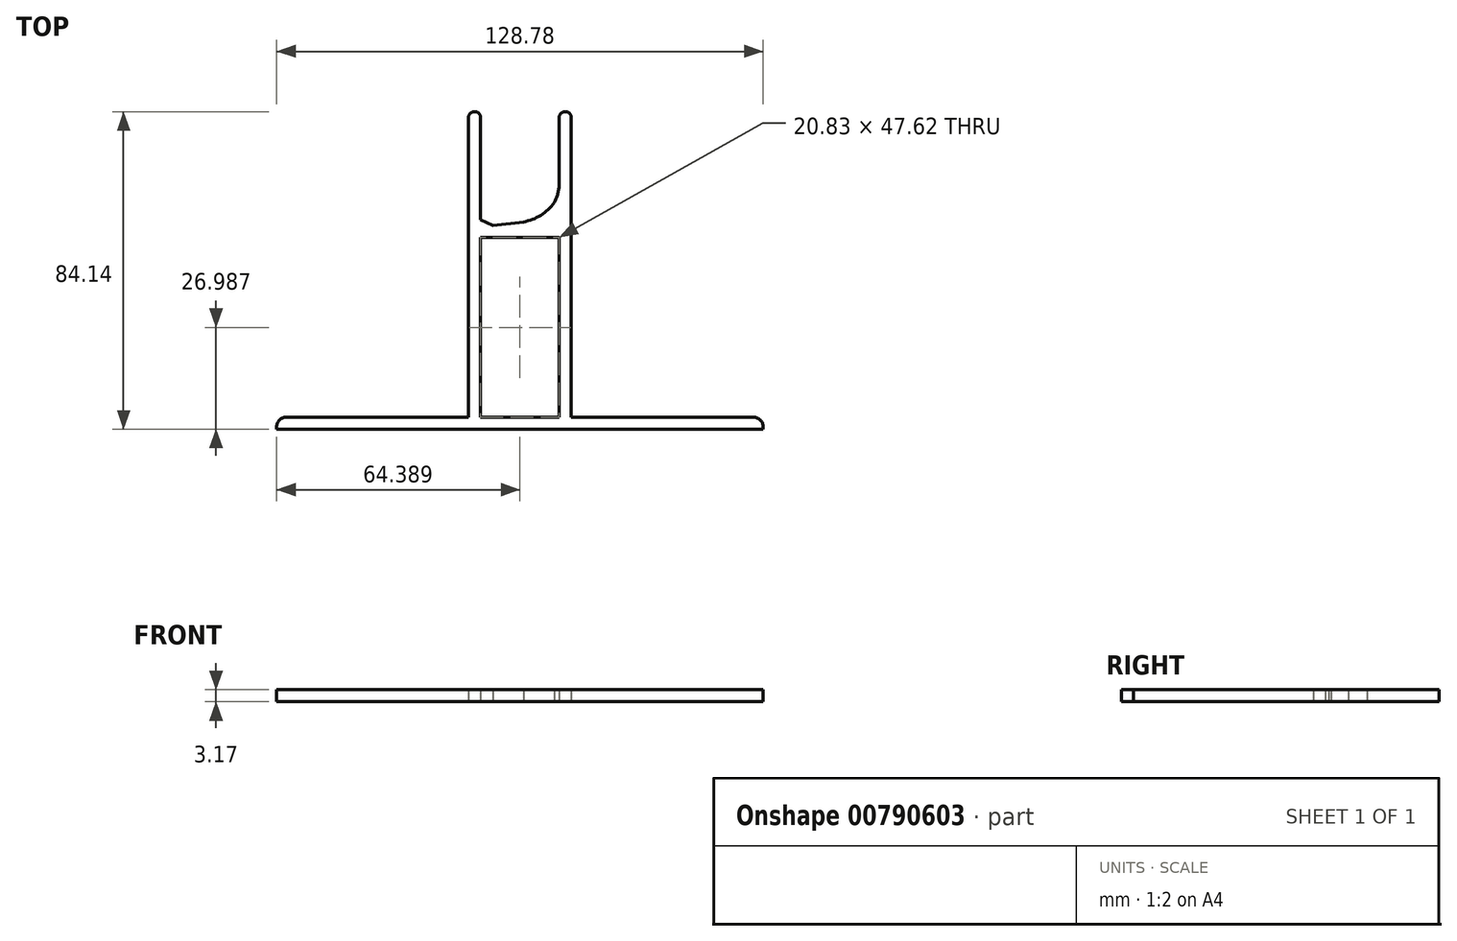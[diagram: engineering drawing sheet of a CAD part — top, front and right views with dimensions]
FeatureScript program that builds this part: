
annotation { "Feature Type Name" : "Feature", "Feature Type Description" : "" }
export const myFeature = defineFeature(function(context is Context, id is Id, definition is map)
    precondition{}
    {
        {
            var Q0;
            Q0=qCreatedBy(makeId("Top.planeOp"),FACE);
            var sketch = newSketch(context, id + "F0", { "sketchPlane" : qUnion([Q0])});
            skLineSegment(sketch, "E0", {"start": v(0, 0) * mm, "end": v(0, 31.75) * mm});
            skLineSegment(sketch, "E1", {"start": v(27.18, 31.75) * mm, "end": v(27.18, 0) * mm});
            skLineSegment(sketch, "E2", {"start": v(27.18, 0) * mm, "end": v(0, 0) * mm});
            skLineSegment(sketch, "E3", {"start": v(3.17, 31.75) * mm, "end": v(3.17, 3.17) * mm});
            skLineSegment(sketch, "E4", {"start": v(3.18, 3.17) * mm, "end": v(24, 3.18) * mm});
            skLineSegment(sketch, "E5", {"start": v(24, 3.18) * mm, "end": v(24, 31.75) * mm});
            skArc(sketch, "E6", {"start": v(0, 31.75) * mm, "mid": v(1.59, 33.34) * mm, "end": v(3.17, 31.75) * mm});
            skArc(sketch, "E7", {"start": v(24, 31.75) * mm, "mid": v(25.6, 33.34) * mm, "end": v(27.18, 31.75) * mm});
            skLineSegment(sketch, "E8", {"start": v(3.18, 4.7) * mm, "end": v(6.48, 3.17) * mm});
            skLineSegment(sketch, "E9", {"start": v(6.48, 3.17) * mm, "end": v(24, 5.2) * mm});
            skArc(sketch, "E10", {"start": v(14.54, 4.11) * mm, "mid": v(20.21, 6.64) * mm, "end": v(24, 11.56) * mm});
            skArc(sketch, "E11", {"start": v(22.7, 9.26) * mm, "mid": v(23.63, 11.64) * mm, "end": v(24, 14.17) * mm});
            skLineSegment(sketch, "E12.bottom", {"start": v(0, 0) * mm, "end": v(27.18, 0) * mm});
            skLineSegment(sketch, "E12.top", {"start": v(0, -50.8) * mm, "end": v(27.18, -50.8) * mm});
            skLineSegment(sketch, "E12.left", {"start": v(0, 0) * mm, "end": v(0, -50.8) * mm});
            skLineSegment(sketch, "E12.right", {"start": v(27.18, 0) * mm, "end": v(27.18, -50.8) * mm});
            skLineSegment(sketch, "E13.bottom", {"start": v(3.18, 0) * mm, "end": v(24, 0) * mm});
            skLineSegment(sketch, "E13.top", {"start": v(3.18, -47.63) * mm, "end": v(24, -47.63) * mm});
            skLineSegment(sketch, "E13.left", {"start": v(3.17, 0) * mm, "end": v(3.18, -47.63) * mm});
            skLineSegment(sketch, "E13.right", {"start": v(24, 0) * mm, "end": v(24, -47.63) * mm});
            skLineSegment(sketch, "E14.bottom", {"start": v(-50.8, -50.8) * mm, "end": v(77.98, -50.8) * mm});
            skLineSegment(sketch, "E14.top", {"start": v(-48.26, -47.63) * mm, "end": v(75.44, -47.63) * mm});
            skLineSegment(sketch, "E14.left", {"start": v(-50.8, -50.8) * mm, "end": v(-50.8, -50.17) * mm});
            skLineSegment(sketch, "E14.right", {"start": v(77.98, -50.8) * mm, "end": v(77.98, -50.17) * mm});
            skPoint(sketch, "E15.visualSharp", {"position": v(-50.8, -47.62) * mm});
            skArc(sketch, "E15.filletArc", {"start": v(-48.26, -47.63) * mm, "mid": v(-50.06, -48.37) * mm, "end": v(-50.8, -50.17) * mm});
            skPoint(sketch, "E16.visualSharp", {"position": v(77.98, -47.63) * mm});
            skArc(sketch, "E16.filletArc", {"start": v(77.98, -50.17) * mm, "mid": v(77.23, -48.37) * mm, "end": v(75.44, -47.63) * mm});
            skSolve(sketch);
        }
        {
            var Q0;
            Q0 = qSketchRegion(id + "F0", true);
            extrude(context, id + "F1", {"entities" : qUnion([Q0]), "depth" : 3.17 * mm, "offsetDistance" : 25.4 * mm});
        }
    });
